FCSTD DOCUMENT  (FreeCAD 1.0R39109 (Git))
Label: board
License: All rights reserved
LicenseURL: https://en.wikipedia.org/wiki/All_rights_reserved
objects: Part::Part2DObjectPython×4
note: 4 computed .brp shape members not serialized (recipe doc carries the construction recipe); baked Part::Feature solids carry a one-line shape summary decoded from their .brp

FEATURE [Part::Part2DObjectPython] Rectangle  # Draft 2D object (typed FeaturePython)
  Area = 0
  ChamferSize = 0
  Columns = 1
  FilletRadius = 0
  Height = 292.3
  Length = 500
  MakeFace = false
  Placement = pos=(-68.4757,-58.5202,0) rot=(0,0,1;0rad)
  Rows = 1
FEATURE [Part::Part2DObjectPython] Line  # Draft 2D object (typed FeaturePython)
  Area = 0
  ChamferSize = 0
  Closed = false
  End = (431.524,-58.5202,0)
  FilletRadius = 0
  Length = 579.171
  MakeFace = true
  Placement = pos=(-68.4757,233.78,0) rot=(0,0,1;0rad)
  Points = (2) [(0,0,0),(500,-292.3,0)]
  Start = (-68.4757,233.78,0)
  Subdivisions = 0
FEATURE [Part::Part2DObjectPython] Circle  # Draft 2D object (typed FeaturePython)
  Area = 0
  FirstAngle = 0
  LastAngle = 0
  MakeFace = false
  Placement = pos=(181.524,87.6298,0) rot=(0,0,1;0rad)
  Radius = 20
FEATURE [Part::Part2DObjectPython] Rectangle001  # Draft 2D object (typed FeaturePython)
  Area = 0
  ChamferSize = 0
  Columns = 1
  FilletRadius = 0
  Height = 47.9593
  Length = 57.2218
  MakeFace = false
  Placement = pos=(151.883,63.6865,0) rot=(0,0,1;0rad)
  Rows = 1
